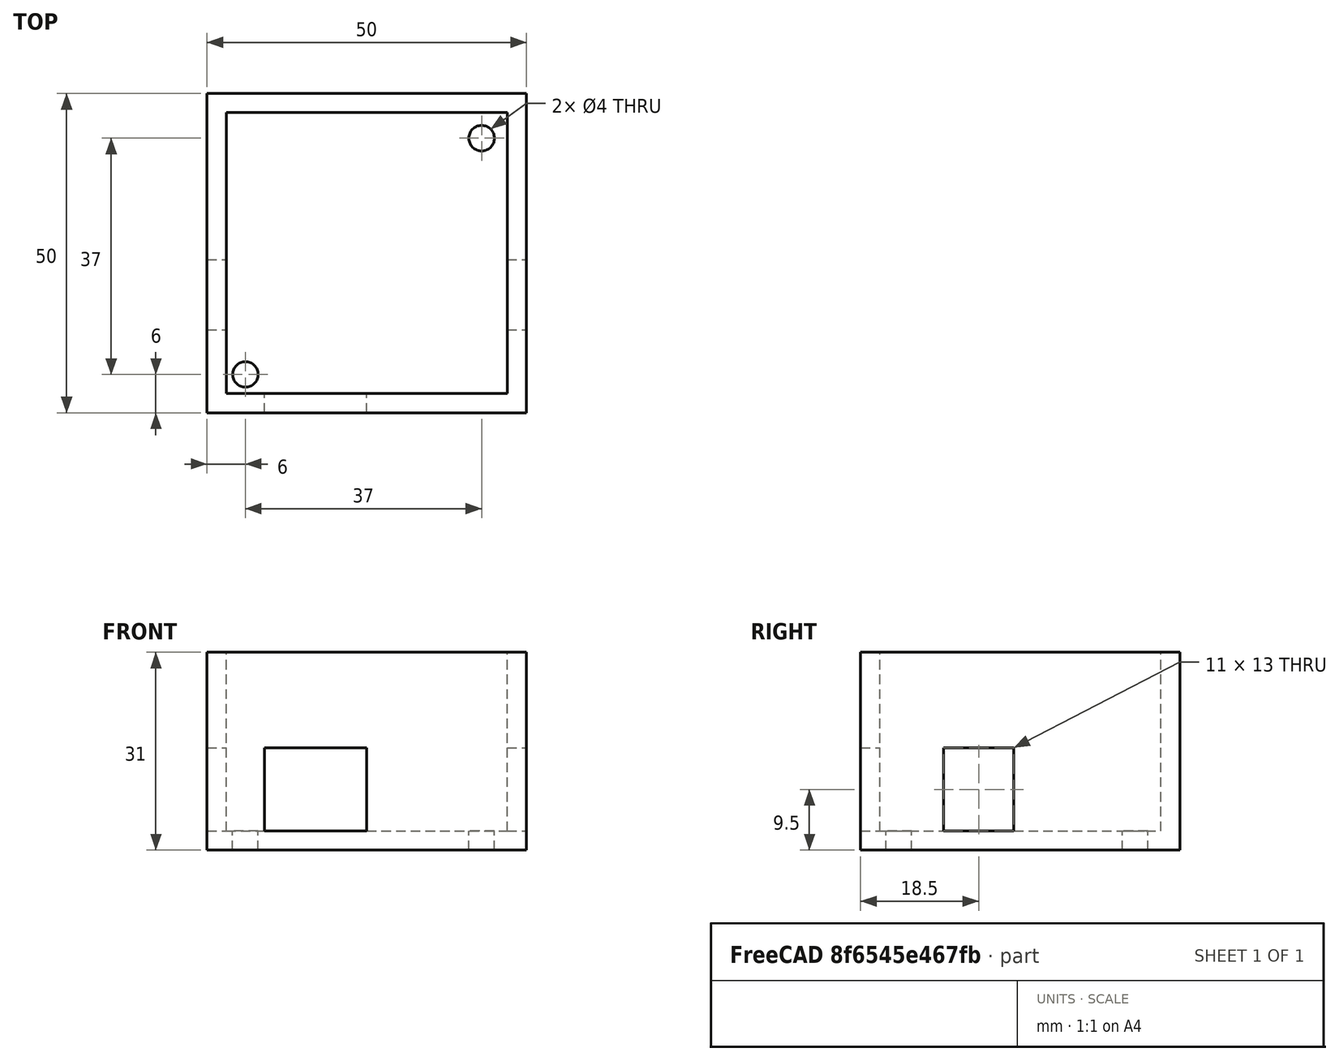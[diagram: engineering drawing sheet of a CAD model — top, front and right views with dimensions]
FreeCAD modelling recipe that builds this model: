
FCSTD DOCUMENT  (FreeCAD 0.19R24291 (Git))
Label: caja_controlador_ruedas
License: All rights reserved
LicenseURL: http://en.wikipedia.org/wiki/All_rights_reserved
objects: Part::Cut×6, Part::Box×4, App::Link×2, Part::Cylinder×1
note: 11 computed .brp shape members not serialized (recipe doc carries the construction recipe); baked Part::Feature solids carry a one-line shape summary decoded from their .brp

FEATURE [Part::Box] Box  label="Cube"
  AttacherType = Attacher::AttachEngine3D
  Height = 31
  Length = 50
  Width = 50
FEATURE [Part::Box] Box001  label="Cube001"
  AttacherType = Attacher::AttachEngine3D
  Height = 29
  Length = 44
  Placement = pos=(3,3,3) rot=(0,0,1;0rad)
  Width = 44
FEATURE [Part::Cut] Cut
  Base = -> Box
  Refine = true
  Tool = -> Box001
FEATURE [Part::Box] Box002  label="Cube002"
  AttacherType = Attacher::AttachEngine3D
  Height = 13
  Length = 16
  Placement = pos=(9,-7,3) rot=(0,0,1;0rad)
  Width = 10
FEATURE [Part::Box] Box003  label="Cube003"
  AttacherType = Attacher::AttachEngine3D
  Height = 13
  Length = 10
  Placement = pos=(-3,13,3) rot=(0,0,1;0rad)
  Width = 11
FEATURE [App::Link] Link  label="Cube004"
  LinkPlacement = pos=(44,13,3) rot=(0,0,1;0rad)
  LinkedObject = -> Box003
  Placement = pos=(44,13,3) rot=(0,0,1;0rad)
FEATURE [Part::Cut] Cut001
  Base = -> Cut
  Refine = true
  Tool = -> Box002
FEATURE [Part::Cut] Cut002
  Base = -> Cut001
  Refine = true
  Tool = -> Box003
FEATURE [Part::Cut] Cut003
  Base = -> Cut002
  Refine = true
  Tool = -> Link
FEATURE [Part::Cylinder] Cylinder
  Angle = 360
  AttacherType = Attacher::AttachEngine3D
  Height = 10
  Placement = pos=(6,6,-1) rot=(0,0,1;0rad)
  Radius = 2
FEATURE [Part::Cut] Cut004
  Base = -> Cut003
  Refine = true
  Tool = -> Cylinder
FEATURE [App::Link] Link001  label="Cylinder001"
  LinkPlacement = pos=(43,43,-1) rot=(0,0,1;0rad)
  LinkedObject = -> Cylinder
  Placement = pos=(43,43,-1) rot=(0,0,1;0rad)
FEATURE [Part::Cut] Cut005
  Base = -> Cut004
  Refine = true
  Tool = -> Link001
